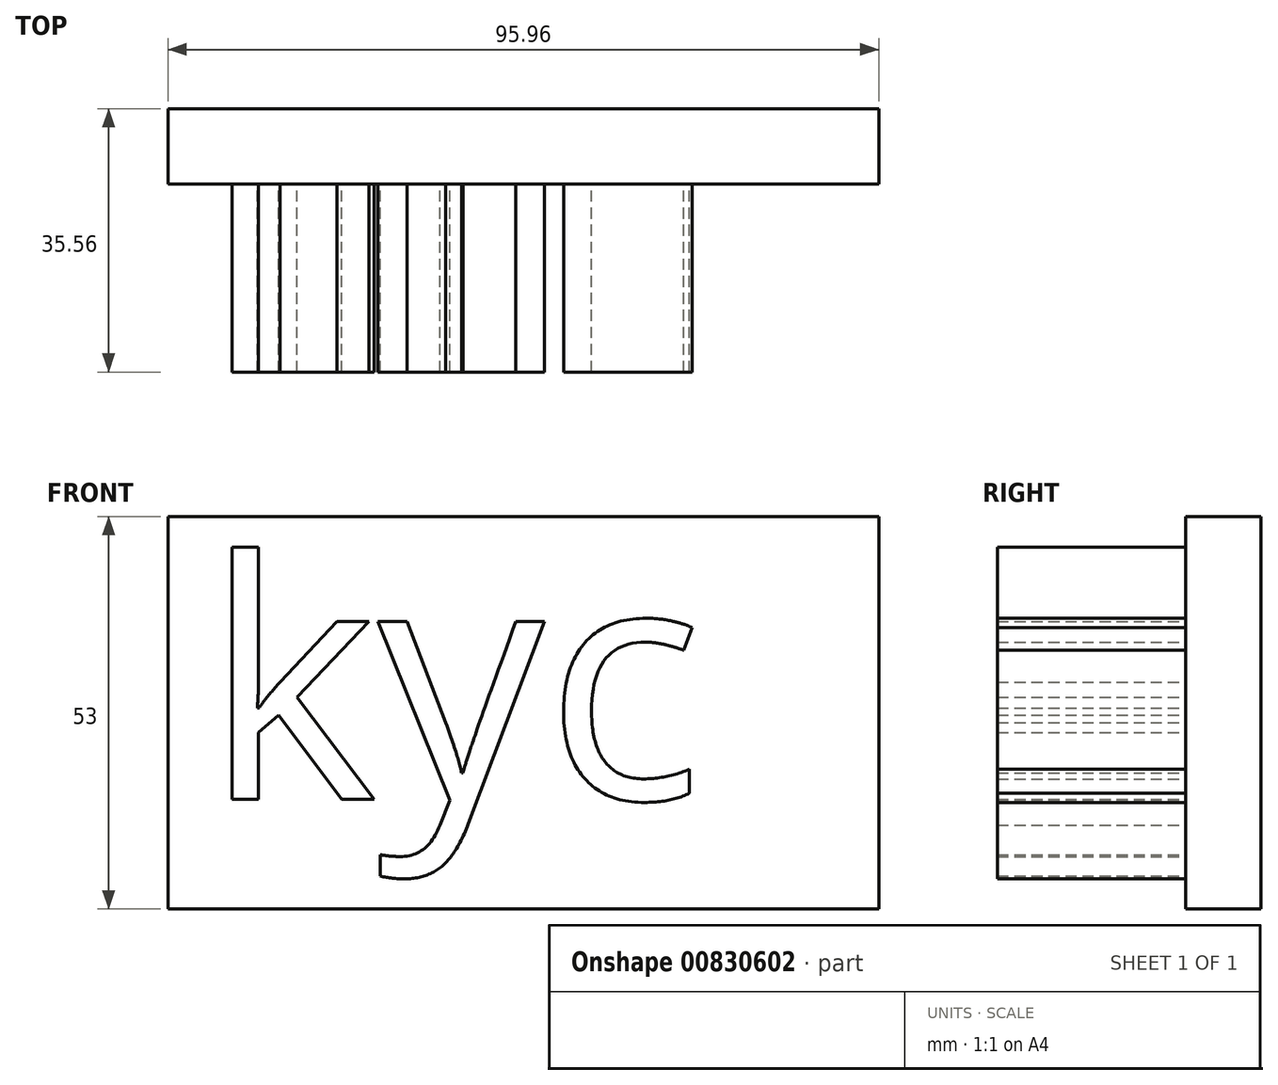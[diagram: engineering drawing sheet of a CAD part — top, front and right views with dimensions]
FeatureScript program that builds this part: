
annotation { "Feature Type Name" : "Feature", "Feature Type Description" : "" }
export const myFeature = defineFeature(function(context is Context, id is Id, definition is map)
    precondition{}
    {
        {
            var Q0;
            Q0=qCreatedBy(makeId("Front.planeOp"),FACE);
            var sketch = newSketch(context, id + "F0", { "sketchPlane" : qUnion([Q0])});
            skLineSegment(sketch, "E0.bottom", {"start": v(0, 0) * mm, "end": v(95.96, 0) * mm});
            skLineSegment(sketch, "E0.top", {"start": v(0, 53) * mm, "end": v(95.96, 53) * mm});
            skLineSegment(sketch, "E0.left", {"start": v(0, 0) * mm, "end": v(0, 53) * mm});
            skLineSegment(sketch, "E0.right", {"start": v(95.96, 0) * mm, "end": v(95.96, 53) * mm});
            skSolve(sketch);
        }
        {
            var Q0;
            Q0=makeQuery(id+"F0.imprint","IMPRINT",FACE,{"disambiguationData":[TD([[makeQuery(id+"F0.imprint","IMPRINT",EDGE,{"derivedFrom":sQuery(id+"F0.wireOp",EDGE,"E0.bottom")}),1.0]])]});
            extrude(context, id + "F1", {"entities" : qUnion([Q0]), "depth" : 10.16 * mm, "offsetDistance" : 25.4 * mm});
        }
        {
            var Q0;
            Q0=makeQuery(id+"F1.opExtrude","CAP_FACE",FACE,{"disambiguationData":[OSD([sQuery(id+"F0.wireOp",EDGE,"E0.bottom"),sQuery(id+"F0.wireOp",EDGE,"E0.top"),sQuery(id+"F0.wireOp",EDGE,"E0.left"),sQuery(id+"F0.wireOp",EDGE,"E0.right")])],"isStart":false});
            var sketch = newSketch(context, id + "F2", { "sketchPlane" : qUnion([Q0])});
            skText(sketch, "E1", { "text": "kyc\n", "fontName": "OpenSans-Regular.ttf"});
            const initialGuessF2  = {"E1": [0.0048, 0.01484, 1, 0, 0.03226]};
            skSetInitialGuess(sketch, initialGuessF2);
            skSolve(sketch);
        }
        {
            var Q0;
            Q0 = qSketchRegion(id + "F2", true);
            extrude(context, id + "F3", {"entities" : qUnion([Q0]), "operationType" : NewBodyOperationType.ADD, "depth" : 25.4 * mm, "offsetDistance" : 25.4 * mm});
        }
    });
